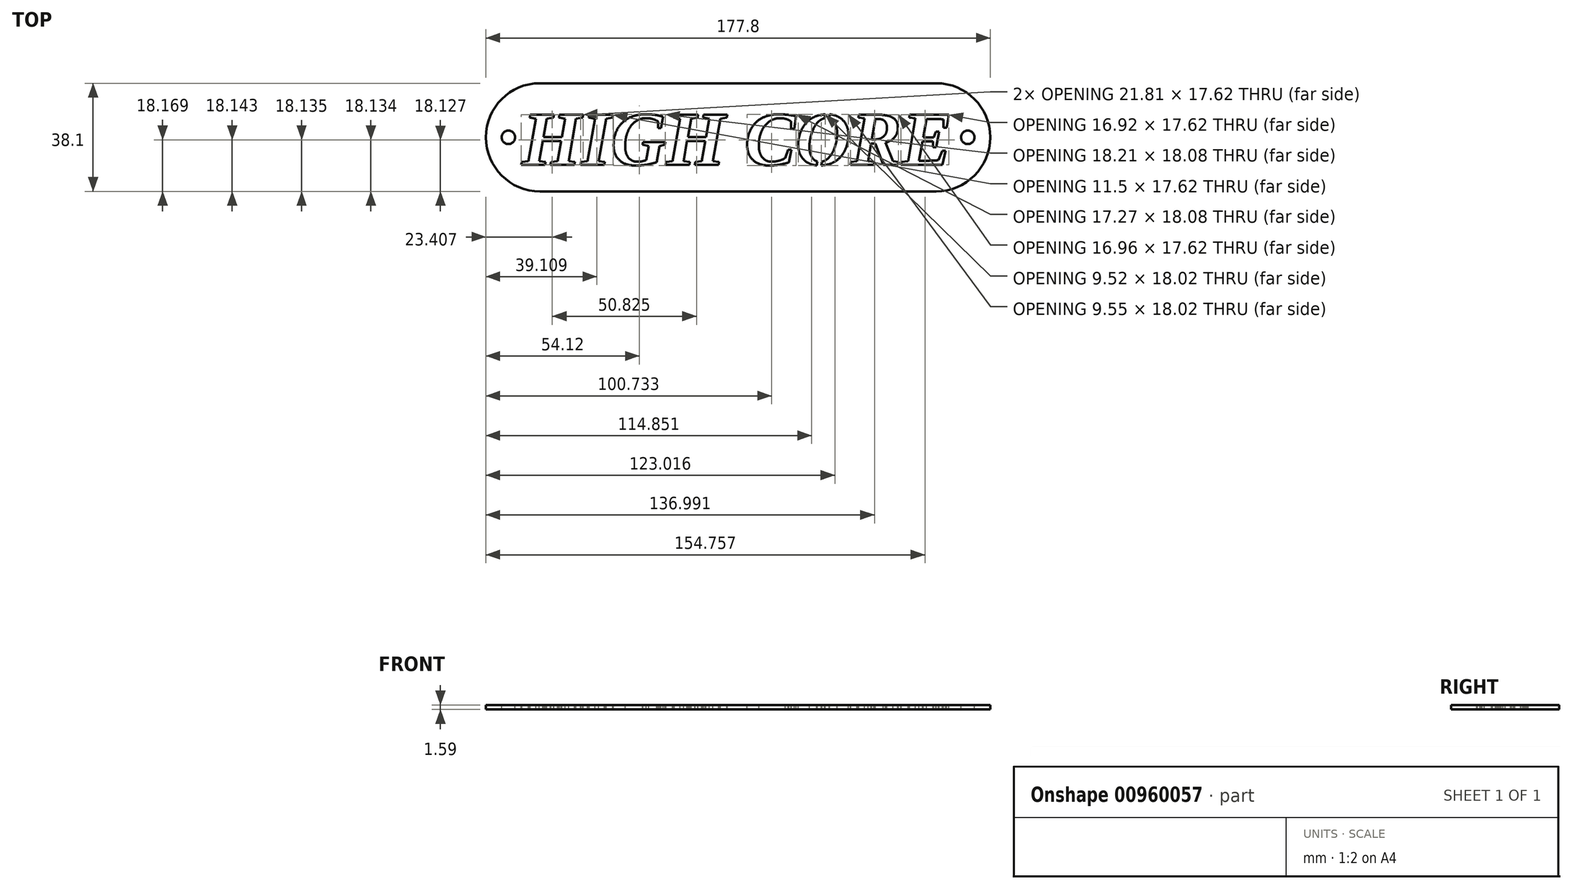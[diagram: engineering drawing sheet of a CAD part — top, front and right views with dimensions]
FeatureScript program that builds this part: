
annotation { "Feature Type Name" : "Feature", "Feature Type Description" : "" }
export const myFeature = defineFeature(function(context is Context, id is Id, definition is map)
    precondition{}
    {
        {
            var Q0;
            Q0=qCreatedBy(makeId("Top.planeOp"),FACE);
            var sketch = newSketch(context, id + "F0", { "sketchPlane" : qUnion([Q0])});
            skLineSegment(sketch, "E0.bottom", {"start": v(88.9, -19.05) * mm, "end": v(-88.9, -19.05) * mm});
            skLineSegment(sketch, "E0.top", {"start": v(88.9, 19.05) * mm, "end": v(-88.9, 19.05) * mm});
            skLineSegment(sketch, "E0.left", {"start": v(88.9, -19.05) * mm, "end": v(88.9, 19.05) * mm});
            skLineSegment(sketch, "E0.right", {"start": v(-88.9, -19.05) * mm, "end": v(-88.9, 19.05) * mm});
            skPoint(sketch, "E0.middle", {"position": v(0, 0) * mm});
            skSolve(sketch);
        }
        {
            var Q0;
            Q0=makeQuery(id+"F0.imprint","IMPRINT",FACE,{"disambiguationData":[TD([[makeQuery(id+"F0.imprint","IMPRINT",EDGE,{"derivedFrom":sQuery(id+"F0.wireOp",EDGE,"E0.bottom")}),-1.0]])]});
            extrude(context, id + "F1", {"entities" : qUnion([Q0]), "depth" : 1.59 * mm, "offsetDistance" : 25.4 * mm});
        }
        {
            var Q0;
            Q0=qCreatedBy(makeId("Top.planeOp"),FACE);
            var sketch = newSketch(context, id + "F2", { "sketchPlane" : qUnion([Q0])});
            skText(sketch, "E1", { "text": "HIGH CORE", "fontName": "Tinos-BoldItalic.ttf"});
            skPoint(sketch, "E2", {"position": v(0, 0) * mm});
            skCircle(sketch, "E3", {"center": v(-80.96, 0) * mm, "radius": 2.38 * mm});
            skCircle(sketch, "E4", {"center": v(80.96, 0) * mm, "radius": 2.38 * mm});
            skLineSegment(sketch, "E5", {"start": v(-80.96, 0) * mm, "end": v(0, 0) * mm, "construction": true});
            skLineSegment(sketch, "E6", {"start": v(0, 0) * mm, "end": v(80.96, 0) * mm, "construction": true});
            skLineSegment(sketch, "E7", {"start": v(32.47, 9.04) * mm, "end": v(28.91, -12.55) * mm});
            skLineSegment(sketch, "E8.0", {"start": v(30.9, 9.3) * mm, "end": v(27.34, -12.3) * mm});
            skLineSegment(sketch, "E9", {"start": v(30.9, 9.3) * mm, "end": v(32.47, 9.04) * mm});
            skLineSegment(sketch, "E10", {"start": v(27.34, -12.3) * mm, "end": v(28.91, -12.55) * mm});
            const initialGuessF2  = {"E1": [-0.0762, -0.00969, 1, 0, 0.01937]};
            skSetInitialGuess(sketch, initialGuessF2);
            skSolve(sketch);
        }
        {
            var Q0;
            Q0=makeQuery(id+"F2.imprint","IMPRINT",FACE,{"disambiguationData":[TD([[makeQuery(id+"F2.imprint","IMPRINT",EDGE,{"derivedFrom":sQuery(id+"F2.wireOp",EDGE,"E1.sketch_text.stroke-93")}),-1.0]])]});
            var Q1;
            {var subQ8=sQuery(id+"F2.wireOp",EDGE,"E1.sketch_text.stroke-119");Q1=makeQuery(id+"F2.imprint","IMPRINT",FACE,{"disambiguationData":[TD([[makeQuery(id+"F2.imprint","IMPRINT",EDGE,{"derivedFrom":subQ8}),-1.0]])]});}
            var Q2;
            {var subQ3=sQuery(id+"F2.wireOp",EDGE,"E1.sketch_text.stroke-116");Q2=makeQuery(id+"F2.imprint","IMPRINT",FACE,{"disambiguationData":[TD([[makeQuery(id+"F2.imprint","IMPRINT",EDGE,{"derivedFrom":subQ3}),-1.0]])]});}
            var Q3;
            Q3=makeQuery(id+"F2.imprint","IMPRINT",FACE,{"disambiguationData":[TD([[makeQuery(id+"F2.imprint","IMPRINT",EDGE,{"derivedFrom":sQuery(id+"F2.wireOp",EDGE,"E1.sketch_text.stroke-138")}),-1.0]])]});
            var Q4;
            Q4=makeQuery(id+"F2.imprint","IMPRINT",FACE,{"disambiguationData":[TD([[makeQuery(id+"F2.imprint","IMPRINT",EDGE,{"derivedFrom":sQuery(id+"F2.wireOp",EDGE,"E1.sketch_text.stroke-165")}),-1.0]])]});
            var Q5;
            Q5=makeQuery(id+"F2.imprint","IMPRINT",FACE,{"disambiguationData":[TD([[makeQuery(id+"F2.imprint","IMPRINT",EDGE,{"derivedFrom":sQuery(id+"F2.wireOp",EDGE,"E1.sketch_text.stroke-65")}),-1.0]])]});
            var Q6;
            Q6=makeQuery(id+"F2.imprint","IMPRINT",FACE,{"disambiguationData":[TD([[makeQuery(id+"F2.imprint","IMPRINT",EDGE,{"derivedFrom":sQuery(id+"F2.wireOp",EDGE,"E1.sketch_text.stroke-40")}),-1.0]])]});
            var Q7;
            Q7=makeQuery(id+"F2.imprint","IMPRINT",FACE,{"disambiguationData":[TD([[makeQuery(id+"F2.imprint","IMPRINT",EDGE,{"derivedFrom":sQuery(id+"F2.wireOp",EDGE,"E1.sketch_text.stroke-28")}),-1.0]])]});
            var Q8;
            Q8=makeQuery(id+"F2.imprint","IMPRINT",FACE,{"disambiguationData":[TD([[makeQuery(id+"F2.imprint","IMPRINT",EDGE,{"derivedFrom":sQuery(id+"F2.wireOp",EDGE,"E1.sketch_text.stroke-0")}),-1.0]])]});
            var Q9;
            Q9=makeQuery(id+"F2.imprint","IMPRINT",FACE,{"disambiguationData":[TD([[makeQuery(id+"F2.imprint","IMPRINT",EDGE,{"derivedFrom":sQuery(id+"F2.wireOp",EDGE,"E3")}),1.0]])]});
            var Q10;
            Q10=makeQuery(id+"F2.imprint","IMPRINT",FACE,{"disambiguationData":[TD([[makeQuery(id+"F2.imprint","IMPRINT",EDGE,{"derivedFrom":sQuery(id+"F2.wireOp",EDGE,"E4")}),1.0]])]});
            extrude(context, id + "F3", {"entities" : qUnion([Q0, Q1, Q2, Q3, Q4, Q5, Q6, Q7, Q8, Q9, Q10]), "operationType" : NewBodyOperationType.REMOVE, "endBound" : BoundingType.SYMMETRIC, "oppositeDirection" : true, "depth" : 25.4 * mm, "offsetDistance" : 25.4 * mm});
        }
        {
            var Q0;
            Q0=makeQuery(id+"F1.opExtrude","SWEPT_EDGE",EDGE,{"disambiguationData":[OSD([sQuery(id+"F0.wireOp",EDGE,"E0.top"),sQuery(id+"F0.wireOp",EDGE,"E0.right")])]});
            var Q1;
            Q1=makeQuery(id+"F1.opExtrude","SWEPT_EDGE",EDGE,{"disambiguationData":[OSD([sQuery(id+"F0.wireOp",EDGE,"E0.bottom"),sQuery(id+"F0.wireOp",EDGE,"E0.right")])]});
            var Q2;
            Q2=makeQuery(id+"F1.opExtrude","SWEPT_EDGE",EDGE,{"disambiguationData":[OSD([sQuery(id+"F0.wireOp",EDGE,"E0.top"),sQuery(id+"F0.wireOp",EDGE,"E0.left")])]});
            var Q3;
            Q3=makeQuery(id+"F1.opExtrude","SWEPT_EDGE",EDGE,{"disambiguationData":[OSD([sQuery(id+"F0.wireOp",EDGE,"E0.bottom"),sQuery(id+"F0.wireOp",EDGE,"E0.left")])]});
            fillet(context, id + "F4", {"entities" : qUnion([Q0, Q1, Q2, Q3]), "radius" : 19.05 * mm, "tangentPropagation" : true, "allowEdgeOverflow" : false});
        }
    });
